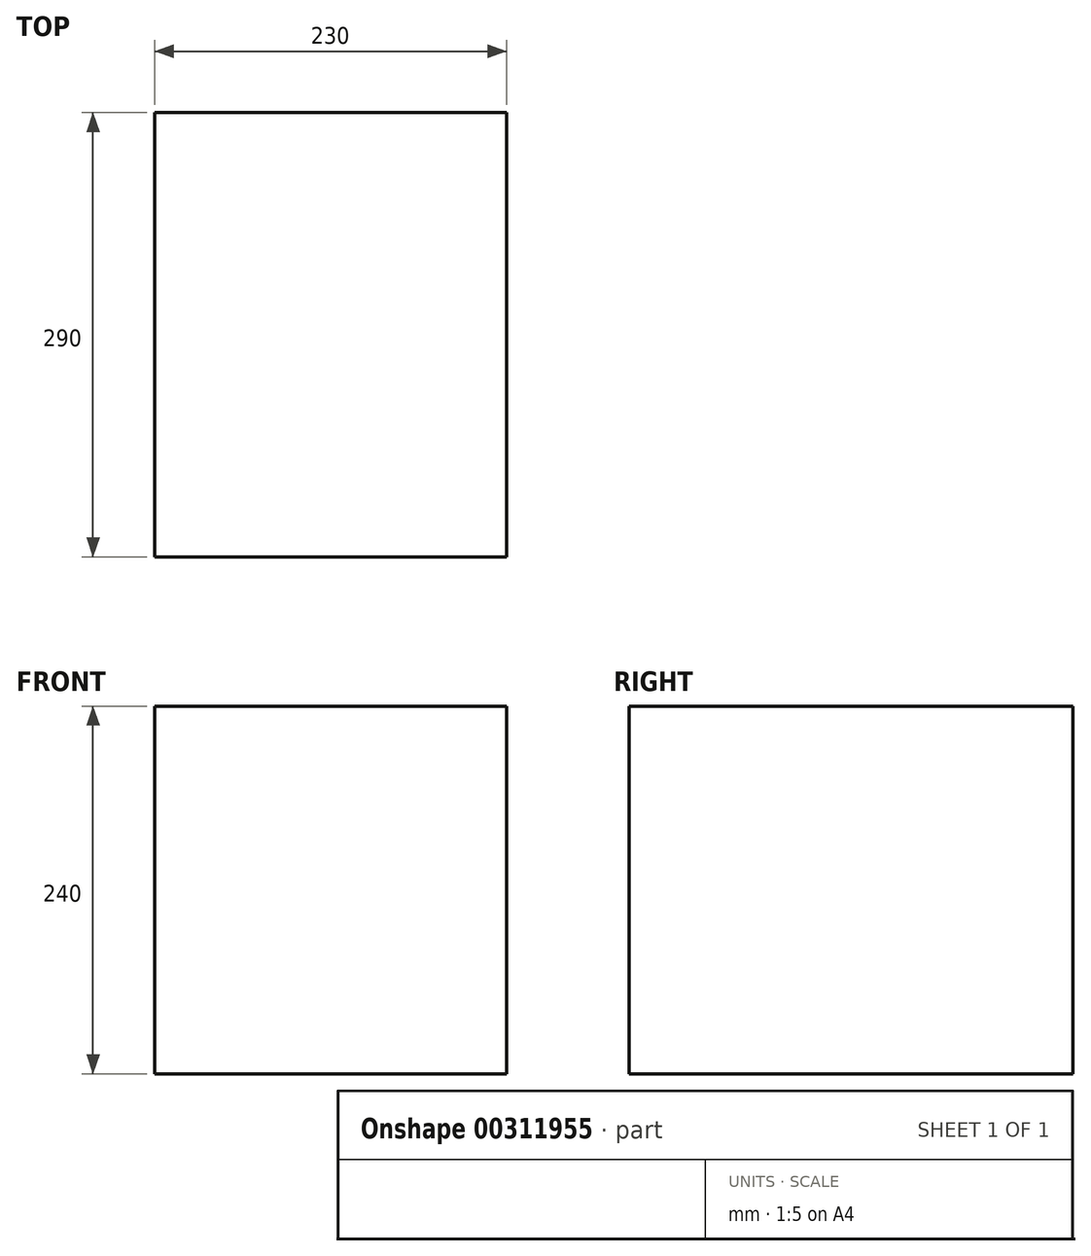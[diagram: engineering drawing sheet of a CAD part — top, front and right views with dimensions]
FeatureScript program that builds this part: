
annotation { "Feature Type Name" : "Feature", "Feature Type Description" : "" }
export const myFeature = defineFeature(function(context is Context, id is Id, definition is map)
    precondition{}
    {
        {
            var Q0;
            Q0=qCreatedBy(makeId("Top.planeOp"),FACE);
            var sketch = newSketch(context, id + "F0", { "sketchPlane" : qUnion([Q0])});
            skLineSegment(sketch, "E0.bottom", {"start": v(115, -145) * mm, "end": v(-115, -145) * mm});
            skLineSegment(sketch, "E0.top", {"start": v(115, 145) * mm, "end": v(-115, 145) * mm});
            skLineSegment(sketch, "E0.left", {"start": v(115, -145) * mm, "end": v(115, 145) * mm});
            skLineSegment(sketch, "E0.right", {"start": v(-115, -145) * mm, "end": v(-115, 145) * mm});
            skPoint(sketch, "E0.middle", {"position": v(0, 0) * mm});
            skSolve(sketch);
        }
        {
            var Q0;
            Q0 = qSketchRegion(id + "F0", true);
            extrude(context, id + "F1", {"entities" : qUnion([Q0]), "depth" : 240 * mm});
        }
    });
